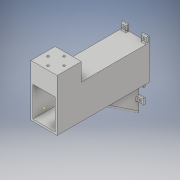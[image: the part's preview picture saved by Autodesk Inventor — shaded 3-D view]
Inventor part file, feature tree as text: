
AUTODESK INVENTOR PART (.ipt)
format: ipt  version: 2019 (Build 230136000, 136)  size: 326,144 bytes
history: native  units: mm
features: sketch x7, extrude x5, fillet x2, projected_geometry x2, other x1, loft x1
ambient origin geometry x8: Origin, YZ Plane, XZ Plane, XY Plane, X Axis, Y Axis, Z Axis, Center Point
bodies: Body1 (feature_tree)
feature tree (18):
  other  "Твердое тело1"
  extrude  "Выдавливание1"  Depth=26.0mm
  sketch  "Эскиз2"
  extrude  "Выдавливание2"  Depth=34.0mm
  extrude  "Выдавливание3"  Depth=2.0mm
  extrude  "Выдавливание4"  Depth=2.0mm
  sketch  "Эскиз4"
  loft  "Лофт1"
  fillet  "Сопряжение1"  Radius=24.0mm
  extrude  "Выдавливание5"  Depth=2.0mm
  fillet  "Сопряжение2"  Radius=2.0mm
  sketch  "Эскиз1"
  projected_geometry  "Спроецированная петля1"
  sketch  "Эскиз3"
  sketch  "Эскиз5"
  sketch  "Эскиз6"
  sketch  "Эскиз7"
  projected_geometry  "Спроецированная петля2"
